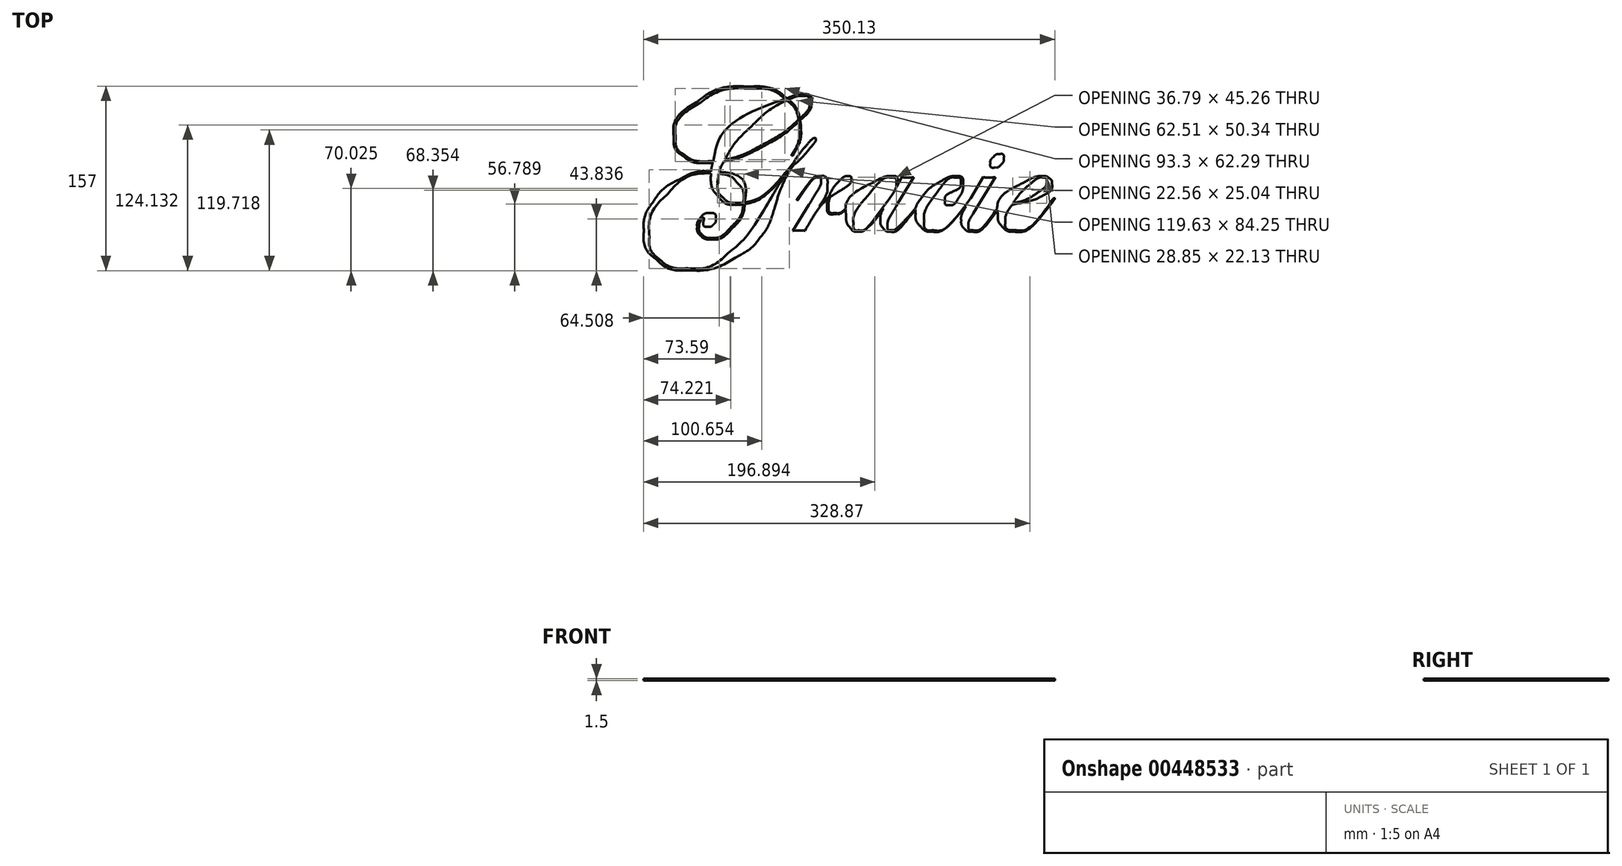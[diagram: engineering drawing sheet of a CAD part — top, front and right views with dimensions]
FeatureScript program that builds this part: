
annotation { "Feature Type Name" : "Feature", "Feature Type Description" : "" }
export const myFeature = defineFeature(function(context is Context, id is Id, definition is map)
    precondition{}
    {
        {
            var Q0;
            Q0=qCreatedBy(makeId("Top.planeOp"),FACE);
            var sketch = newSketch(context, id + "F0", { "sketchPlane" : qUnion([Q0])});
            skFitSpline(sketch, "E0", {"points": [v(-28.46, 33.84) * mm, v(-28.46, 32.45) * mm, v(-30.63, 29.2) * mm, v(-34.96, 24.09) * mm]});
            skFitSpline(sketch, "E1", {"points": [v(-34.96, 24.09) * mm, v(-39.24, 19.03) * mm, v(-43.58, 14.64) * mm, v(-47.97, 10.92) * mm]});
            skFitSpline(sketch, "E2", {"points": [v(-47.97, 10.92) * mm, v(-51.91, 4.58) * mm, v(-54.8, -0.67) * mm, v(-56.64, -4.83) * mm]});
            skFitSpline(sketch, "E3", {"points": [v(-56.64, -4.83) * mm, v(-58.47, -8.95) * mm, v(-60.75, -15.48) * mm, v(-63.47, -24.42) * mm]});
            skFitSpline(sketch, "E4", {"points": [v(-63.47, -24.42) * mm, v(-66.86, -35.31) * mm, v(-71.05, -43.95) * mm, v(-76.06, -50.34) * mm]});
            skFitSpline(sketch, "E5", {"points": [v(-76.06, -50.34) * mm, v(-81, -56.73) * mm, v(-87.97, -62.43) * mm, v(-96.98, -67.43) * mm]});
            skFitSpline(sketch, "E6", {"points": [v(-96.98, -67.43) * mm, v(-109.87, -74.6) * mm, v(-123.06, -78.18) * mm, v(-136.57, -78.18) * mm]});
            skFitSpline(sketch, "E7", {"points": [v(-136.57, -78.18) * mm, v(-148.01, -78.18) * mm, v(-157.27, -75.07) * mm, v(-164.32, -68.85) * mm]});
            skFitSpline(sketch, "E8", {"points": [v(-164.32, -68.85) * mm, v(-171.38, -62.62) * mm, v(-174.9, -54.45) * mm, v(-174.9, -44.34) * mm]});
            skFitSpline(sketch, "E9", {"points": [v(-174.9, -44.34) * mm, v(-174.9, -35.73) * mm, v(-172.24, -27.56) * mm, v(-166.9, -19.84) * mm]});
            skFitSpline(sketch, "E10", {"points": [v(-166.9, -19.84) * mm, v(-161.57, -12.06) * mm, v(-154.3, -5.78) * mm, v(-145.07, -1) * mm]});
            skFitSpline(sketch, "E11", {"points": [v(-145.07, -1) * mm, v(-135.79, 3.78) * mm, v(-127.2, 6.17) * mm, v(-119.31, 6.17) * mm]});
            skFitSpline(sketch, "E12", {"points": [v(-119.31, 6.17) * mm, v(-118.65, 6.17) * mm, v(-118.06, 6.11) * mm, v(-117.56, 6) * mm]});
            skFitSpline(sketch, "E13", {"points": [v(-117.56, 6) * mm, v(-117.56, 7.4) * mm, v(-117.17, 9.84) * mm, v(-116.4, 13.34) * mm]});
            skFitSpline(sketch, "E14", {"points": [v(-116.4, 13.34) * mm, v(-117.4, 13.22) * mm, v(-118.6, 13.17) * mm, v(-119.98, 13.17) * mm]});
            skFitSpline(sketch, "E15", {"points": [v(-119.98, 13.17) * mm, v(-128.93, 13.17) * mm, v(-136.07, 15.14) * mm, v(-141.4, 19.09) * mm]});
            skFitSpline(sketch, "E16", {"points": [v(-141.4, 19.09) * mm, v(-146.68, 23.03) * mm, v(-149.32, 28.28) * mm, v(-149.32, 34.84) * mm]});
            skFitSpline(sketch, "E17", {"points": [v(-149.32, 34.84) * mm, v(-149.32, 46.18) * mm, v(-142.9, 56.23) * mm, v(-130.07, 65.01) * mm]});
            skFitSpline(sketch, "E18", {"points": [v(-130.07, 65.01) * mm, v(-117.23, 73.8) * mm, v(-102.48, 78.18) * mm, v(-85.8, 78.18) * mm]});
            skFitSpline(sketch, "E19", {"points": [v(-85.8, 78.18) * mm, v(-72.58, 78.18) * mm, v(-61.78, 74.88) * mm, v(-53.39, 68.26) * mm]});
            skFitSpline(sketch, "E20", {"points": [v(-53.39, 68.26) * mm, v(-47.55, 70.43) * mm, v(-43.24, 71.51) * mm, v(-40.47, 71.51) * mm]});
            skFitSpline(sketch, "E21", {"points": [v(-40.47, 71.51) * mm, v(-35.08, 71.51) * mm, v(-32.38, 69.3) * mm, v(-32.38, 64.85) * mm]});
            skFitSpline(sketch, "E22", {"points": [v(-32.38, 64.85) * mm, v(-32.38, 60.73) * mm, v(-35.52, 55.62) * mm, v(-41.8, 49.5) * mm]});
            skFitSpline(sketch, "E23", {"points": [v(-41.8, 49.5) * mm, v(-41.35, 46.45) * mm, v(-41.13, 43.9) * mm, v(-41.13, 41.84) * mm]});
            skFitSpline(sketch, "E24", {"points": [v(-41.13, 41.84) * mm, v(-41.13, 35.84) * mm, v(-42.88, 29.42) * mm, v(-46.38, 22.59) * mm]});
            skFitSpline(sketch, "E25", {"points": [v(-46.38, 22.59) * mm, v(-47.44, 20.53) * mm, v(-48.19, 19.5) * mm, v(-48.63, 19.5) * mm]});
            skFitSpline(sketch, "E26", {"points": [v(-48.63, 19.5) * mm, v(-48.91, 19.5) * mm, v(-49.08, 19.67) * mm, v(-49.13, 20) * mm]});
            skFitSpline(sketch, "E27", {"points": [v(-49.13, 20) * mm, v(-49.08, 20.28) * mm, v(-48.97, 20.56) * mm, v(-48.8, 20.84) * mm]});
            skFitSpline(sketch, "E28", {"points": [v(-48.8, 20.84) * mm, v(-44.69, 27.62) * mm, v(-42.63, 34.73) * mm, v(-42.63, 42.17) * mm]});
            skFitSpline(sketch, "E29", {"points": [v(-42.63, 42.17) * mm, v(-42.63, 44.45) * mm, v(-42.74, 46.56) * mm, v(-42.97, 48.5) * mm]});
            skFitSpline(sketch, "E30", {"points": [v(-42.97, 48.5) * mm, v(-52.25, 40.34) * mm, v(-62.6, 33.2) * mm, v(-74.06, 27.09) * mm]});
            skFitSpline(sketch, "E31", {"points": [v(-74.06, 27.09) * mm, v(-85.45, 21.03) * mm, v(-96.3, 16.84) * mm, v(-106.64, 14.5) * mm]});
            skFitSpline(sketch, "E32", {"points": [v(-106.64, 14.5) * mm, v(-108.42, 11.61) * mm, v(-109.78, 8.61) * mm, v(-110.73, 5.5) * mm]});
            skFitSpline(sketch, "E33", {"points": [v(-110.73, 5.5) * mm, v(-96.06, 3) * mm, v(-88.72, -4.97) * mm, v(-88.72, -18.42) * mm]});
            skFitSpline(sketch, "E34", {"points": [v(-88.72, -20.09) * mm, v(-77.67, -17.09) * mm, v(-64.08, -6.11) * mm, v(-47.97, 12.84) * mm]});
            skFitSpline(sketch, "E35", {"points": [v(-47.97, 12.84) * mm, v(-44.36, 18.5) * mm, v(-40.66, 23.5) * mm, v(-36.88, 27.84) * mm]});
            skFitSpline(sketch, "E36", {"points": [v(-36.88, 27.84) * mm, v(-33.1, 32.17) * mm, v(-30.52, 34.34) * mm, v(-29.13, 34.34) * mm]});
            skFitSpline(sketch, "E37", {"points": [v(-29.13, 34.34) * mm, v(-28.8, 34.34) * mm, v(-28.57, 34.17) * mm, v(-28.46, 33.84) * mm]});
            skLineSegment(sketch, "E38", {"start": v(-88.72, -18.42) * mm, "end": v(-88.72, -20.09) * mm});
            skFitSpline(sketch, "E39", {"points": [v(-33.96, 64.68) * mm, v(-33.96, 68.35) * mm, v(-36.08, 70.18) * mm, v(-40.3, 70.18) * mm]});
            skFitSpline(sketch, "E40", {"points": [v(-40.3, 70.18) * mm, v(-43.52, 70.18) * mm, v(-47.38, 69.1) * mm, v(-51.88, 66.93) * mm]});
            skFitSpline(sketch, "E41", {"points": [v(-51.88, 66.93) * mm, v(-47.1, 62.82) * mm, v(-43.86, 57.54) * mm, v(-42.13, 51.1) * mm]});
            skFitSpline(sketch, "E42", {"points": [v(-42.13, 51.1) * mm, v(-36.69, 56.37) * mm, v(-33.96, 60.9) * mm, v(-33.96, 64.68) * mm]});
            skFitSpline(sketch, "E43", {"points": [v(-43.3, 50) * mm, v(-44.74, 56.62) * mm, v(-48.05, 62.1) * mm, v(-53.22, 66.43) * mm]});
            skFitSpline(sketch, "E44", {"points": [v(-53.22, 66.43) * mm, v(-63.16, 61.48) * mm, v(-73.06, 54.29) * mm, v(-82.9, 44.84) * mm]});
            skFitSpline(sketch, "E45", {"points": [v(-82.9, 44.84) * mm, v(-92.73, 35.45) * mm, v(-100.37, 25.87) * mm, v(-105.81, 16.09) * mm]});
            skFitSpline(sketch, "E46", {"points": [v(-105.81, 16.09) * mm, v(-95.92, 18.42) * mm, v(-85.3, 22.64) * mm, v(-73.97, 28.76) * mm]});
            skFitSpline(sketch, "E47", {"points": [v(-73.97, 28.76) * mm, v(-62.58, 34.92) * mm, v(-52.36, 42) * mm, v(-43.3, 50) * mm]});
            skFitSpline(sketch, "E48", {"points": [v(-54.97, 67.76) * mm, v(-62.36, 73.6) * mm, v(-72.53, 76.51) * mm, v(-85.47, 76.51) * mm]});
            skFitSpline(sketch, "E49", {"points": [v(-85.47, 76.51) * mm, v(-101.09, 76.51) * mm, v(-115.4, 72.18) * mm, v(-128.4, 63.51) * mm]});
            skFitSpline(sketch, "E50", {"points": [v(-128.4, 63.51) * mm, v(-141.35, 54.9) * mm, v(-147.82, 45.4) * mm, v(-147.82, 35) * mm]});
            skFitSpline(sketch, "E51", {"points": [v(-147.82, 35) * mm, v(-147.82, 28.62) * mm, v(-145.26, 23.62) * mm, v(-140.15, 20) * mm]});
            skFitSpline(sketch, "E52", {"points": [v(-140.15, 20) * mm, v(-135.04, 16.45) * mm, v(-127.93, 14.67) * mm, v(-118.81, 14.67) * mm]});
            skFitSpline(sketch, "E53", {"points": [v(-115.9, 14.67) * mm, v(-109.4, 35.95) * mm, v(-89.09, 53.65) * mm, v(-54.97, 67.76) * mm]});
            skLineSegment(sketch, "E54", {"start": v(-118.81, 14.67) * mm, "end": v(-115.9, 14.67) * mm});
            skFitSpline(sketch, "E55", {"points": [v(-90.14, -20.5) * mm, v(-89.75, -13.9) * mm, v(-91.4, -8.45) * mm, v(-95.06, -4.17) * mm]});
            skFitSpline(sketch, "E56", {"points": [v(-95.06, -4.17) * mm, v(-98.73, 0.17) * mm, v(-104, 2.92) * mm, v(-110.9, 4.08) * mm]});
            skFitSpline(sketch, "E57", {"points": [v(-110.9, 4.08) * mm, v(-111.73, 1.25) * mm, v(-112.15, -1.58) * mm, v(-112.15, -4.42) * mm]});
            skFitSpline(sketch, "E58", {"points": [v(-112.15, -4.42) * mm, v(-112.15, -9.36) * mm, v(-110.56, -13.34) * mm, v(-107.4, -16.34) * mm]});
            skFitSpline(sketch, "E59", {"points": [v(-107.4, -16.34) * mm, v(-104.17, -19.34) * mm, v(-99.95, -20.84) * mm, v(-94.73, -20.84) * mm]});
            skFitSpline(sketch, "E60", {"points": [v(-94.73, -20.84) * mm, v(-93.11, -20.84) * mm, v(-91.59, -20.73) * mm, v(-90.14, -20.5) * mm]});
            skFitSpline(sketch, "E61", {"points": [v(-50.88, 7.5) * mm, v(-65.83, -9.11) * mm, v(-78.56, -18.84) * mm, v(-89.06, -21.67) * mm]});
            skFitSpline(sketch, "E62", {"points": [v(-89.06, -21.67) * mm, v(-90.17, -29.28) * mm, v(-93.75, -36.23) * mm, v(-99.81, -42.5) * mm]});
            skFitSpline(sketch, "E63", {"points": [v(-99.81, -42.5) * mm, v(-105.81, -48.73) * mm, v(-111.9, -51.84) * mm, v(-118.06, -51.84) * mm]});
            skFitSpline(sketch, "E64", {"points": [v(-118.06, -51.84) * mm, v(-121.34, -51.84) * mm, v(-124.1, -50.84) * mm, v(-126.32, -48.84) * mm]});
            skFitSpline(sketch, "E65", {"points": [v(-126.32, -48.84) * mm, v(-128.48, -46.84) * mm, v(-129.57, -44.37) * mm, v(-129.57, -41.42) * mm]});
            skFitSpline(sketch, "E66", {"points": [v(-129.57, -41.42) * mm, v(-129.57, -38.37) * mm, v(-128.54, -35.62) * mm, v(-126.48, -33.17) * mm]});
            skFitSpline(sketch, "E67", {"points": [v(-126.48, -33.17) * mm, v(-124.37, -30.73) * mm, v(-122.04, -29.5) * mm, v(-119.48, -29.5) * mm]});
            skFitSpline(sketch, "E68", {"points": [v(-119.48, -29.5) * mm, v(-115.6, -29.5) * mm, v(-113.65, -31.28) * mm, v(-113.65, -34.84) * mm]});
            skFitSpline(sketch, "E69", {"points": [v(-113.65, -34.84) * mm, v(-113.65, -36.45) * mm, v(-114.29, -37.9) * mm, v(-115.56, -39.17) * mm]});
            skFitSpline(sketch, "E70", {"points": [v(-115.56, -39.17) * mm, v(-116.84, -40.45) * mm, v(-118.26, -41.1) * mm, v(-119.81, -41.1) * mm]});
            skFitSpline(sketch, "E71", {"points": [v(-119.81, -41.1) * mm, v(-122.76, -41.1) * mm, v(-124.23, -39.79) * mm, v(-124.23, -37.17) * mm]});
            skFitSpline(sketch, "E72", {"points": [v(-124.23, -37.17) * mm, v(-124.23, -36.78) * mm, v(-124.12, -36.17) * mm, v(-123.9, -35.34) * mm]});
            skFitSpline(sketch, "E73", {"points": [v(-123.9, -35.34) * mm, v(-123.79, -34.9) * mm, v(-123.73, -34.48) * mm, v(-123.73, -34.09) * mm]});
            skFitSpline(sketch, "E74", {"points": [v(-123.73, -34.09) * mm, v(-123.73, -33.76) * mm, v(-123.9, -33.59) * mm, v(-124.23, -33.59) * mm]});
            skFitSpline(sketch, "E75", {"points": [v(-124.23, -33.59) * mm, v(-125.07, -33.59) * mm, v(-125.9, -34.5) * mm, v(-126.73, -36.34) * mm]});
            skFitSpline(sketch, "E76", {"points": [v(-126.73, -36.34) * mm, v(-127.57, -38.12) * mm, v(-127.98, -39.81) * mm, v(-127.98, -41.42) * mm]});
            skFitSpline(sketch, "E77", {"points": [v(-127.98, -41.42) * mm, v(-127.98, -44.04) * mm, v(-127.04, -46.2) * mm, v(-125.15, -47.93) * mm]});
            skFitSpline(sketch, "E78", {"points": [v(-125.15, -47.93) * mm, v(-123.26, -49.65) * mm, v(-120.9, -50.5) * mm, v(-118.06, -50.5) * mm]});
            skFitSpline(sketch, "E79", {"points": [v(-118.06, -50.5) * mm, v(-112.4, -50.5) * mm, v(-106.59, -47.43) * mm, v(-100.64, -41.26) * mm]});
            skFitSpline(sketch, "E80", {"points": [v(-100.64, -41.26) * mm, v(-94.64, -35.09) * mm, v(-91.25, -28.67) * mm, v(-90.48, -22) * mm]});
            skFitSpline(sketch, "E81", {"points": [v(-90.48, -22) * mm, v(-91.7, -22.23) * mm, v(-93.11, -22.34) * mm, v(-94.73, -22.34) * mm]});
            skFitSpline(sketch, "E82", {"points": [v(-94.73, -22.34) * mm, v(-101.84, -22.34) * mm, v(-107.45, -19.95) * mm, v(-111.56, -15.17) * mm]});
            skFitSpline(sketch, "E83", {"points": [v(-111.56, -15.17) * mm, v(-115.67, -10.34) * mm, v(-117.73, -3.8) * mm, v(-117.73, 4.42) * mm]});
            skFitSpline(sketch, "E84", {"points": [v(-117.73, 4.42) * mm, v(-131.73, 3.53) * mm, v(-143.99, -2.3) * mm, v(-154.49, -13.09) * mm]});
            skFitSpline(sketch, "E85", {"points": [v(-154.49, -13.09) * mm, v(-164.93, -23.81) * mm, v(-170.16, -35.9) * mm, v(-170.16, -49.34) * mm]});
            skFitSpline(sketch, "E86", {"points": [v(-170.16, -49.34) * mm, v(-170.16, -57.4) * mm, v(-167.18, -63.93) * mm, v(-161.24, -68.93) * mm]});
            skFitSpline(sketch, "E87", {"points": [v(-161.24, -68.93) * mm, v(-155.24, -73.93) * mm, v(-147.4, -76.43) * mm, v(-137.73, -76.43) * mm]});
            skFitSpline(sketch, "E88", {"points": [v(-137.73, -76.43) * mm, v(-124.62, -76.43) * mm, v(-112.7, -71.8) * mm, v(-101.98, -62.51) * mm]});
            skFitSpline(sketch, "E89", {"points": [v(-101.98, -62.51) * mm, v(-91.25, -53.23) * mm, v(-78.8, -36.78) * mm, v(-64.64, -13.17) * mm]});
            skFitSpline(sketch, "E90", {"points": [v(-64.64, -13.17) * mm, v(-60.3, -5.83) * mm, v(-55.72, 1.06) * mm, v(-50.88, 7.5) * mm]});
            skFitSpline(sketch, "E91", {"points": [v(4.38, -17.25) * mm, v(4.38, -17.7) * mm, v(2.7, -19.73) * mm, v(-0.63, -23.34) * mm]});
            skFitSpline(sketch, "E92", {"points": [v(-0.63, -23.34) * mm, v(-4.85, -28) * mm, v(-8.82, -30.34) * mm, v(-12.54, -30.34) * mm]});
            skFitSpline(sketch, "E93", {"points": [v(-12.54, -30.34) * mm, v(-16.77, -30.34) * mm, v(-18.88, -27.9) * mm, v(-18.88, -23) * mm]});
            skFitSpline(sketch, "E94", {"points": [v(-18.88, -23) * mm, v(-18.88, -21.45) * mm, v(-18.55, -19.48) * mm, v(-17.88, -17.09) * mm]});
            skFitSpline(sketch, "E95", {"points": [v(-17.88, -17.09) * mm, v(-21.38, -20.14) * mm, v(-24.24, -23.17) * mm, v(-26.46, -26.17) * mm]});
            skFitSpline(sketch, "E96", {"points": [v(-26.46, -26.17) * mm, v(-28.63, -29.17) * mm, v(-32.4, -35.28) * mm, v(-37.8, -44.5) * mm]});
            skFitSpline(sketch, "E97", {"points": [v(-37.8, -44.5) * mm, v(-40.74, -44.29) * mm, v(-42.47, -44.17) * mm, v(-42.97, -44.17) * mm]});
            skFitSpline(sketch, "E98", {"points": [v(-42.97, -44.17) * mm, v(-43.19, -44.17) * mm, v(-44.88, -44.29) * mm, v(-48.05, -44.5) * mm]});
            skFitSpline(sketch, "E99", {"points": [v(-34.38, -22.34) * mm, v(-27.55, -11.22) * mm, v(-24.13, -4.33) * mm, v(-24.13, -1.67) * mm]});
            skFitSpline(sketch, "E100", {"points": [v(-24.13, -1.67) * mm, v(-24.13, -0.11) * mm, v(-24.77, 0.67) * mm, v(-26.05, 0.67) * mm]});
            skFitSpline(sketch, "E101", {"points": [v(-26.05, 0.67) * mm, v(-29.16, 0.67) * mm, v(-34.8, -5.3) * mm, v(-42.97, -17.25) * mm]});
            skFitSpline(sketch, "E102", {"points": [v(-42.97, -17.25) * mm, v(-43.47, -18.03) * mm, v(-43.91, -18.42) * mm, v(-44.3, -18.42) * mm]});
            skFitSpline(sketch, "E103", {"points": [v(-44.3, -18.42) * mm, v(-44.52, -18.36) * mm, v(-44.63, -18.2) * mm, v(-44.63, -17.92) * mm]});
            skFitSpline(sketch, "E104", {"points": [v(-44.63, -17.92) * mm, v(-44.58, -17.64) * mm, v(-44.47, -17.42) * mm, v(-44.3, -17.25) * mm]});
            skLineSegment(sketch, "E105", {"start": v(-48.05, -44.5) * mm, "end": v(-34.38, -22.34) * mm});
            skFitSpline(sketch, "E106", {"points": [v(-42.8, -15.17) * mm, v(-34.24, -3.78) * mm, v(-28.44, 1.92) * mm, v(-25.38, 1.92) * mm]});
            skFitSpline(sketch, "E107", {"points": [v(-25.38, 1.92) * mm, v(-20.93, 1.92) * mm, v(-18.71, -0.94) * mm, v(-18.71, -6.67) * mm]});
            skFitSpline(sketch, "E108", {"points": [v(-18.71, -6.67) * mm, v(-18.71, -10.95) * mm, v(-21, -16.61) * mm, v(-25.55, -23.67) * mm]});
            skFitSpline(sketch, "E109", {"points": [v(-25.55, -23.67) * mm, v(-22.66, -20.34) * mm, v(-19.9, -17.61) * mm, v(-17.3, -15.5) * mm]});
            skFitSpline(sketch, "E110", {"points": [v(-17.3, -15.5) * mm, v(-15.18, -10.56) * mm, v(-12.57, -6.42) * mm, v(-9.46, -3.08) * mm]});
            skFitSpline(sketch, "E111", {"points": [v(-9.46, -3.08) * mm, v(-6.3, 0.25) * mm, v(-3.46, 1.92) * mm, v(-0.96, 1.92) * mm]});
            skFitSpline(sketch, "E112", {"points": [v(-0.96, 1.92) * mm, v(0.76, 1.92) * mm, v(1.63, 1.17) * mm, v(1.63, -0.33) * mm]});
            skFitSpline(sketch, "E113", {"points": [v(1.63, -0.33) * mm, v(1.63, -3) * mm, v(-2.24, -6.8) * mm, v(-9.96, -11.75) * mm]});
            skFitSpline(sketch, "E114", {"points": [v(-9.96, -11.75) * mm, v(-11.18, -12.53) * mm, v(-13.02, -13.67) * mm, v(-15.46, -15.17) * mm]});
            skLineSegment(sketch, "E115", {"start": v(-44.3, -17.25) * mm, "end": v(-42.8, -15.17) * mm});
            skFitSpline(sketch, "E116", {"points": [v(-16.46, -16) * mm, v(-17.24, -18.56) * mm, v(-17.63, -20.67) * mm, v(-17.63, -22.34) * mm]});
            skFitSpline(sketch, "E117", {"points": [v(-17.63, -22.34) * mm, v(-17.63, -27) * mm, v(-15.88, -29.34) * mm, v(-12.38, -29.34) * mm]});
            skFitSpline(sketch, "E118", {"points": [v(-12.38, -29.34) * mm, v(-8.04, -29.34) * mm, v(-3.32, -25.75) * mm, v(1.8, -18.59) * mm]});
            skFitSpline(sketch, "E119", {"points": [v(1.8, -18.59) * mm, v(2.9, -17.36) * mm, v(3.6, -16.75) * mm, v(3.88, -16.75) * mm]});
            skFitSpline(sketch, "E120", {"points": [v(3.88, -16.75) * mm, v(4.2, -16.75) * mm, v(4.38, -16.92) * mm, v(4.38, -17.25) * mm]});
            skLineSegment(sketch, "E121", {"start": v(-15.46, -15.17) * mm, "end": v(-16.46, -16) * mm});
            skFitSpline(sketch, "E122", {"points": [v(62.8, -17.25) * mm, v(62.8, -18.42) * mm, v(58.75, -23.81) * mm, v(50.63, -33.42) * mm]});
            skFitSpline(sketch, "E123", {"points": [v(50.63, -33.42) * mm, v(44.08, -41.31) * mm, v(38.91, -45.26) * mm, v(35.13, -45.26) * mm]});
            skFitSpline(sketch, "E124", {"points": [v(35.13, -45.26) * mm, v(32.58, -45.26) * mm, v(30.5, -44.31) * mm, v(28.88, -42.42) * mm]});
            skFitSpline(sketch, "E125", {"points": [v(28.88, -42.42) * mm, v(27.27, -40.48) * mm, v(26.46, -38.06) * mm, v(26.46, -35.17) * mm]});
            skFitSpline(sketch, "E126", {"points": [v(26.46, -35.17) * mm, v(26.46, -32.17) * mm, v(27.35, -28.92) * mm, v(29.13, -25.42) * mm]});
            skFitSpline(sketch, "E127", {"points": [v(29.13, -25.42) * mm, v(23.57, -33.2) * mm, v(19.32, -38.45) * mm, v(16.38, -41.17) * mm]});
            skFitSpline(sketch, "E128", {"points": [v(16.38, -41.17) * mm, v(13.43, -43.9) * mm, v(10.57, -45.26) * mm, v(7.8, -45.26) * mm]});
            skFitSpline(sketch, "E129", {"points": [v(7.8, -45.26) * mm, v(4.85, -45.26) * mm, v(2.38, -44) * mm, v(0.38, -41.5) * mm]});
            skFitSpline(sketch, "E130", {"points": [v(0.38, -41.5) * mm, v(-1.63, -38.95) * mm, v(-2.63, -35.76) * mm, v(-2.63, -31.92) * mm]});
            skFitSpline(sketch, "E131", {"points": [v(-2.63, -31.92) * mm, v(-2.63, -21.25) * mm, v(4.9, -11.8) * mm, v(19.96, -3.58) * mm]});
            skFitSpline(sketch, "E132", {"points": [v(19.96, -3.58) * mm, v(26.57, 0.08) * mm, v(31.9, 1.92) * mm, v(35.97, 1.92) * mm]});
            skFitSpline(sketch, "E133", {"points": [v(35.97, 1.92) * mm, v(39.41, 1.92) * mm, v(41.13, 0.25) * mm, v(41.13, -3.08) * mm]});
            skFitSpline(sketch, "E134", {"points": [v(41.13, -3.08) * mm, v(41.13, -4.03) * mm, v(40.91, -5.28) * mm, v(40.47, -6.83) * mm]});
            skFitSpline(sketch, "E135", {"points": [v(44.72, 1.25) * mm, v(46.38, 0.86) * mm, v(47.86, 0.67) * mm, v(49.13, 0.67) * mm]});
            skFitSpline(sketch, "E136", {"points": [v(49.13, 0.67) * mm, v(50.63, 0.67) * mm, v(52.58, 0.86) * mm, v(54.97, 1.25) * mm]});
            skLineSegment(sketch, "E137", {"start": v(40.47, -6.83) * mm, "end": v(44.72, 1.25) * mm});
            skFitSpline(sketch, "E138", {"points": [v(40.22, -23.17) * mm, v(35.1, -31.73) * mm, v(32.55, -37.37) * mm, v(32.55, -40.1) * mm]});
            skFitSpline(sketch, "E139", {"points": [v(32.55, -40.1) * mm, v(32.55, -42.7) * mm, v(33.63, -44) * mm, v(35.8, -44) * mm]});
            skFitSpline(sketch, "E140", {"points": [v(35.8, -44) * mm, v(38.02, -44) * mm, v(41.58, -41.48) * mm, v(46.47, -36.42) * mm]});
            skFitSpline(sketch, "E141", {"points": [v(46.47, -36.42) * mm, v(51.36, -31.31) * mm, v(56.33, -25.03) * mm, v(61.39, -17.59) * mm]});
            skFitSpline(sketch, "E142", {"points": [v(61.39, -17.59) * mm, v(61.72, -17.03) * mm, v(62.03, -16.75) * mm, v(62.3, -16.75) * mm]});
            skFitSpline(sketch, "E143", {"points": [v(62.3, -16.75) * mm, v(62.64, -16.75) * mm, v(62.8, -16.92) * mm, v(62.8, -17.25) * mm]});
            skLineSegment(sketch, "E144", {"start": v(54.97, 1.25) * mm, "end": v(40.22, -23.17) * mm});
            skFitSpline(sketch, "E145", {"points": [v(39.88, -3.42) * mm, v(39.88, -0.7) * mm, v(38.63, 0.67) * mm, v(36.13, 0.67) * mm]});
            skFitSpline(sketch, "E146", {"points": [v(36.13, 0.67) * mm, v(31.02, 0.67) * mm, v(24.3, -4.33) * mm, v(15.96, -14.34) * mm]});
            skFitSpline(sketch, "E147", {"points": [v(15.96, -14.34) * mm, v(7.68, -24.34) * mm, v(3.54, -32.42) * mm, v(3.54, -38.6) * mm]});
            skFitSpline(sketch, "E148", {"points": [v(3.54, -38.6) * mm, v(3.54, -42.2) * mm, v(5.15, -44) * mm, v(8.38, -44) * mm]});
            skFitSpline(sketch, "E149", {"points": [v(8.38, -44) * mm, v(12.21, -44) * mm, v(18.85, -37.65) * mm, v(28.3, -24.92) * mm]});
            skFitSpline(sketch, "E150", {"points": [v(28.3, -24.92) * mm, v(36.02, -14.47) * mm, v(39.88, -7.3) * mm, v(39.88, -3.42) * mm]});
            skFitSpline(sketch, "E151", {"points": [v(104.23, -17.25) * mm, v(104.23, -17.98) * mm, v(100.31, -22.64) * mm, v(92.48, -31.26) * mm]});
            skFitSpline(sketch, "E152", {"points": [v(92.48, -31.26) * mm, v(83.92, -40.6) * mm, v(76.64, -45.26) * mm, v(70.64, -45.26) * mm]});
            skFitSpline(sketch, "E153", {"points": [v(70.64, -45.26) * mm, v(66.75, -45.26) * mm, v(63.41, -43.79) * mm, v(60.64, -40.84) * mm]});
            skFitSpline(sketch, "E154", {"points": [v(60.64, -40.84) * mm, v(57.86, -37.84) * mm, v(56.47, -34.28) * mm, v(56.47, -30.17) * mm]});
            skFitSpline(sketch, "E155", {"points": [v(56.47, -30.17) * mm, v(56.47, -25.5) * mm, v(58.36, -20.67) * mm, v(62.14, -15.67) * mm]});
            skFitSpline(sketch, "E156", {"points": [v(62.14, -15.67) * mm, v(65.92, -10.67) * mm, v(71, -6.36) * mm, v(77.39, -2.75) * mm]});
            skFitSpline(sketch, "E157", {"points": [v(77.39, -2.75) * mm, v(82.78, 0.36) * mm, v(87.17, 1.92) * mm, v(90.56, 1.92) * mm]});
            skFitSpline(sketch, "E158", {"points": [v(90.56, 1.92) * mm, v(94.67, 1.92) * mm, v(96.73, -0.53) * mm, v(96.73, -5.42) * mm]});
            skFitSpline(sketch, "E159", {"points": [v(96.73, -5.42) * mm, v(96.73, -9.25) * mm, v(95.42, -13.09) * mm, v(92.8, -16.92) * mm]});
            skFitSpline(sketch, "E160", {"points": [v(92.8, -16.92) * mm, v(90.25, -20.75) * mm, v(87.7, -22.67) * mm, v(85.14, -22.67) * mm]});
            skFitSpline(sketch, "E161", {"points": [v(85.14, -22.67) * mm, v(82.64, -22.67) * mm, v(81.4, -21.42) * mm, v(81.4, -18.92) * mm]});
            skFitSpline(sketch, "E162", {"points": [v(81.4, -18.92) * mm, v(81.4, -15.98) * mm, v(83.95, -13.25) * mm, v(89.06, -10.75) * mm]});
            skFitSpline(sketch, "E163", {"points": [v(89.06, -10.75) * mm, v(93, -8.8) * mm, v(94.98, -6.25) * mm, v(94.98, -3.08) * mm]});
            skFitSpline(sketch, "E164", {"points": [v(94.98, -3.08) * mm, v(94.98, -0.58) * mm, v(93.61, 0.67) * mm, v(90.9, 0.67) * mm]});
            skFitSpline(sketch, "E165", {"points": [v(90.9, 0.67) * mm, v(86.28, 0.67) * mm, v(80.61, -3.92) * mm, v(73.89, -13.09) * mm]});
            skFitSpline(sketch, "E166", {"points": [v(73.89, -13.09) * mm, v(67.17, -22.25) * mm, v(63.8, -29.95) * mm, v(63.8, -36.17) * mm]});
            skFitSpline(sketch, "E167", {"points": [v(63.8, -36.17) * mm, v(63.8, -41.4) * mm, v(66.25, -44) * mm, v(71.14, -44) * mm]});
            skFitSpline(sketch, "E168", {"points": [v(71.14, -44) * mm, v(78.8, -44) * mm, v(89.2, -35.37) * mm, v(102.31, -18.09) * mm]});
            skFitSpline(sketch, "E169", {"points": [v(102.31, -18.09) * mm, v(103.03, -17.2) * mm, v(103.56, -16.75) * mm, v(103.9, -16.75) * mm]});
            skFitSpline(sketch, "E170", {"points": [v(103.9, -16.75) * mm, v(104.12, -16.8) * mm, v(104.23, -16.98) * mm, v(104.23, -17.25) * mm]});
            skFitSpline(sketch, "E171", {"points": [v(131.57, 17.25) * mm, v(131.57, 15.3) * mm, v(130.73, 13.47) * mm, v(129.07, 11.75) * mm]});
            skFitSpline(sketch, "E172", {"points": [v(129.07, 11.75) * mm, v(127.45, 10.09) * mm, v(125.68, 9.25) * mm, v(123.73, 9.25) * mm]});
            skFitSpline(sketch, "E173", {"points": [v(123.73, 9.25) * mm, v(121.23, 9.25) * mm, v(119.98, 10.5) * mm, v(119.98, 13) * mm]});
            skFitSpline(sketch, "E174", {"points": [v(119.98, 13) * mm, v(119.98, 14.84) * mm, v(120.84, 16.59) * mm, v(122.56, 18.25) * mm]});
            skFitSpline(sketch, "E175", {"points": [v(122.56, 18.25) * mm, v(124.29, 19.98) * mm, v(126.1, 20.84) * mm, v(127.98, 20.84) * mm]});
            skFitSpline(sketch, "E176", {"points": [v(127.98, 20.84) * mm, v(130.37, 20.84) * mm, v(131.57, 19.64) * mm, v(131.57, 17.25) * mm]});
            skFitSpline(sketch, "E177", {"points": [v(132.73, -17.25) * mm, v(132.68, -17.42) * mm, v(132.4, -17.86) * mm, v(131.9, -18.59) * mm]});
            skFitSpline(sketch, "E178", {"points": [v(128.32, -23.5) * mm, v(117.87, -38) * mm, v(109.9, -45.26) * mm, v(104.4, -45.26) * mm]});
            skFitSpline(sketch, "E179", {"points": [v(104.4, -45.26) * mm, v(101.78, -45.26) * mm, v(99.59, -44.34) * mm, v(97.8, -42.5) * mm]});
            skFitSpline(sketch, "E180", {"points": [v(97.8, -42.5) * mm, v(96.09, -40.62) * mm, v(95.23, -38.28) * mm, v(95.23, -35.5) * mm]});
            skFitSpline(sketch, "E181", {"points": [v(95.23, -35.5) * mm, v(95.23, -32.28) * mm, v(97.14, -27.4) * mm, v(100.98, -20.84) * mm]});
            skLineSegment(sketch, "E182", {"start": v(131.9, -18.59) * mm, "end": v(128.32, -23.5) * mm});
            skFitSpline(sketch, "E183", {"points": [v(113.98, 1.25) * mm, v(115.7, 0.86) * mm, v(117.06, 0.67) * mm, v(118.06, 0.67) * mm]});
            skFitSpline(sketch, "E184", {"points": [v(118.06, 0.67) * mm, v(119.56, 0.67) * mm, v(121.68, 0.86) * mm, v(124.4, 1.25) * mm]});
            skLineSegment(sketch, "E185", {"start": v(100.98, -20.84) * mm, "end": v(113.98, 1.25) * mm});
            skFitSpline(sketch, "E186", {"points": [v(105.48, -29.84) * mm, v(102.76, -34.34) * mm, v(101.4, -37.81) * mm, v(101.4, -40.26) * mm]});
            skFitSpline(sketch, "E187", {"points": [v(101.4, -40.26) * mm, v(101.4, -42.76) * mm, v(102.7, -44) * mm, v(105.31, -44) * mm]});
            skFitSpline(sketch, "E188", {"points": [v(105.31, -44) * mm, v(110.26, -44) * mm, v(118.95, -35.2) * mm, v(131.4, -17.59) * mm]});
            skFitSpline(sketch, "E189", {"points": [v(131.4, -17.59) * mm, v(131.68, -17.03) * mm, v(131.96, -16.75) * mm, v(132.23, -16.75) * mm]});
            skFitSpline(sketch, "E190", {"points": [v(132.23, -16.75) * mm, v(132.57, -16.75) * mm, v(132.73, -16.92) * mm, v(132.73, -17.25) * mm]});
            skLineSegment(sketch, "E191", {"start": v(124.4, 1.25) * mm, "end": v(105.48, -29.84) * mm});
            skFitSpline(sketch, "E192", {"points": [v(174.9, -17.25) * mm, v(174.9, -17.42) * mm, v(174.4, -18.14) * mm, v(173.4, -19.42) * mm]});
            skFitSpline(sketch, "E193", {"points": [v(169.82, -23.92) * mm, v(158.32, -38.15) * mm, v(148.46, -45.26) * mm, v(140.23, -45.26) * mm]});
            skFitSpline(sketch, "E194", {"points": [v(140.23, -45.26) * mm, v(136.34, -45.26) * mm, v(133.07, -43.87) * mm, v(130.4, -41.1) * mm]});
            skFitSpline(sketch, "E195", {"points": [v(130.4, -41.1) * mm, v(127.79, -38.26) * mm, v(126.48, -34.73) * mm, v(126.48, -30.5) * mm]});
            skFitSpline(sketch, "E196", {"points": [v(126.48, -30.5) * mm, v(126.48, -20.5) * mm, v(133.46, -11.7) * mm, v(147.4, -4.08) * mm]});
            skFitSpline(sketch, "E197", {"points": [v(147.4, -4.08) * mm, v(154.74, -0.08) * mm, v(160.71, 1.92) * mm, v(165.32, 1.92) * mm]});
            skFitSpline(sketch, "E198", {"points": [v(165.32, 1.92) * mm, v(167.32, 1.92) * mm, v(169.02, 1.3) * mm, v(170.4, 0.08) * mm]});
            skFitSpline(sketch, "E199", {"points": [v(170.4, 0.08) * mm, v(171.85, -1.08) * mm, v(172.57, -2.53) * mm, v(172.57, -4.25) * mm]});
            skFitSpline(sketch, "E200", {"points": [v(172.57, -4.25) * mm, v(172.57, -8.25) * mm, v(169.96, -11.67) * mm, v(164.74, -14.5) * mm]});
            skFitSpline(sketch, "E201", {"points": [v(164.74, -14.5) * mm, v(159.52, -17.28) * mm, v(150.8, -19.9) * mm, v(138.57, -22.34) * mm]});
            skFitSpline(sketch, "E202", {"points": [v(138.57, -22.34) * mm, v(134.79, -28.06) * mm, v(132.9, -32.84) * mm, v(132.9, -36.67) * mm]});
            skFitSpline(sketch, "E203", {"points": [v(132.9, -36.67) * mm, v(132.9, -41.45) * mm, v(135.48, -43.84) * mm, v(140.65, -43.84) * mm]});
            skFitSpline(sketch, "E204", {"points": [v(140.65, -43.84) * mm, v(149.43, -43.84) * mm, v(160.18, -35.26) * mm, v(172.9, -18.09) * mm]});
            skFitSpline(sketch, "E205", {"points": [v(172.9, -18.09) * mm, v(173.57, -17.2) * mm, v(174.13, -16.75) * mm, v(174.57, -16.75) * mm]});
            skFitSpline(sketch, "E206", {"points": [v(174.57, -16.75) * mm, v(174.8, -16.8) * mm, v(174.9, -16.98) * mm, v(174.9, -17.25) * mm]});
            skLineSegment(sketch, "E207", {"start": v(173.4, -19.42) * mm, "end": v(169.82, -23.92) * mm});
            skFitSpline(sketch, "E208", {"points": [v(167.9, -1.83) * mm, v(167.9, -0.06) * mm, v(166.93, 0.83) * mm, v(164.99, 0.83) * mm]});
            skFitSpline(sketch, "E209", {"points": [v(164.99, 0.83) * mm, v(162.04, 0.83) * mm, v(158.15, -1.22) * mm, v(153.32, -5.33) * mm]});
            skFitSpline(sketch, "E210", {"points": [v(153.32, -5.33) * mm, v(148.54, -9.4) * mm, v(143.85, -14.67) * mm, v(139.23, -21.17) * mm]});
            skFitSpline(sketch, "E211", {"points": [v(139.23, -21.17) * mm, v(147.24, -19.11) * mm, v(154.01, -16.23) * mm, v(159.57, -12.5) * mm]});
            skFitSpline(sketch, "E212", {"points": [v(159.57, -12.5) * mm, v(165.13, -8.72) * mm, v(167.9, -5.17) * mm, v(167.9, -1.83) * mm]});
            skSolve(sketch);
        }
        {
            var Q0;
            Q0 = qSketchRegion(id + "F0", true);
            extrude(context, id + "F1", {"entities" : qUnion([Q0]), "depth" : 1.5 * mm});
        }
    });
